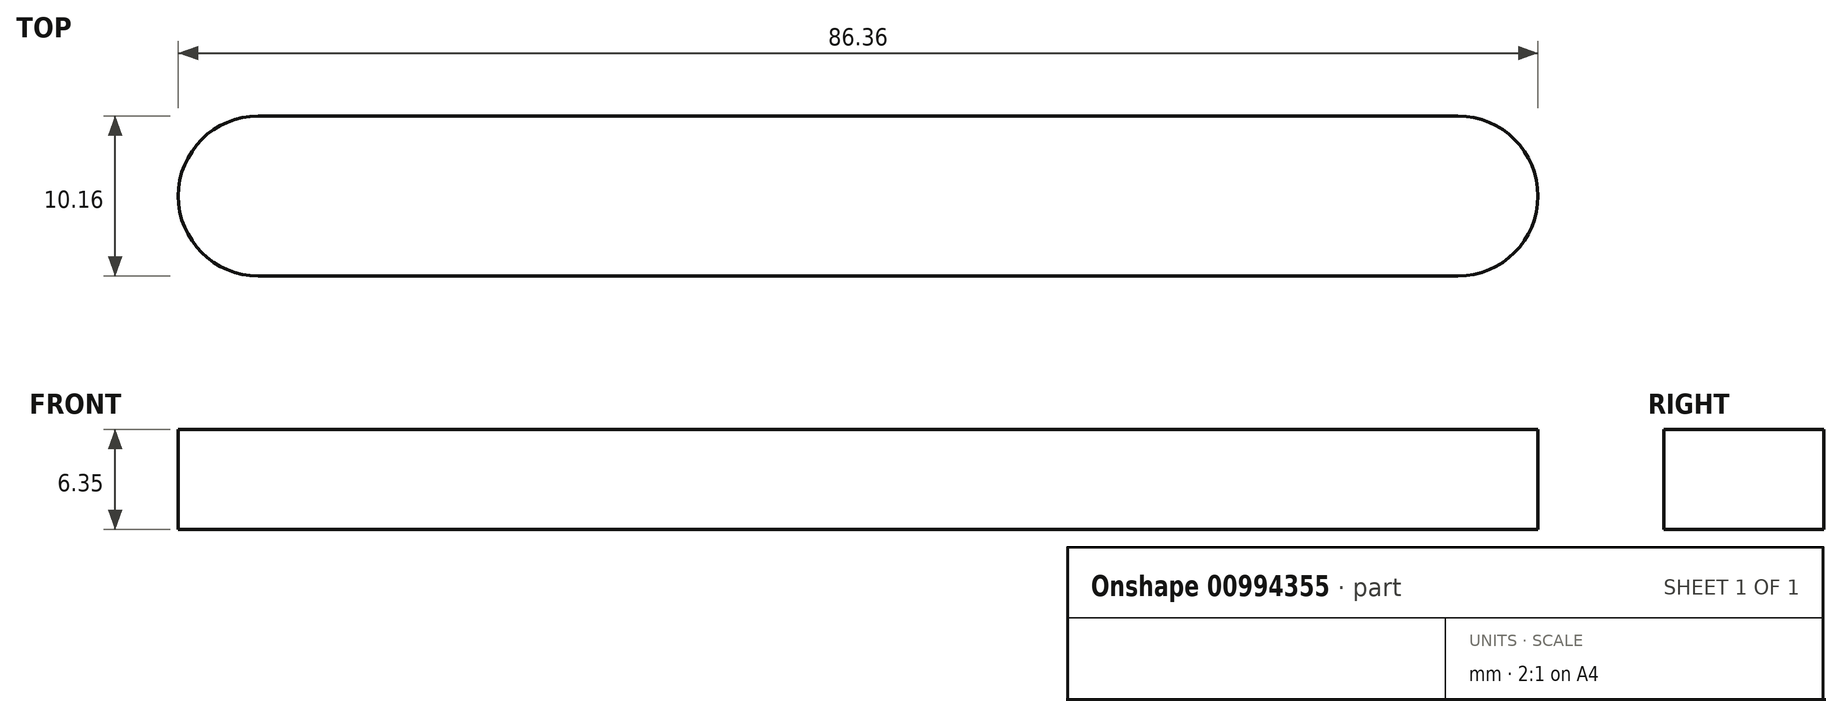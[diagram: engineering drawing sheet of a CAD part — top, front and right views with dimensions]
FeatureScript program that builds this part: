
annotation { "Feature Type Name" : "Feature", "Feature Type Description" : "" }
export const myFeature = defineFeature(function(context is Context, id is Id, definition is map)
    precondition{}
    {
        {
            var Q0;
            Q0=qCreatedBy(makeId("Top.planeOp"),FACE);
            var sketch = newSketch(context, id + "F0", { "sketchPlane" : qUnion([Q0])});
            skLineSegment(sketch, "E0.bottom", {"start": v(-50.8, 12.7) * mm, "end": v(50.8, 12.7) * mm});
            skLineSegment(sketch, "E0.top", {"start": v(-50.8, -12.7) * mm, "end": v(50.8, -12.7) * mm});
            skLineSegment(sketch, "E0.left", {"start": v(-50.8, 12.7) * mm, "end": v(-50.8, -12.7) * mm});
            skLineSegment(sketch, "E0.right", {"start": v(50.8, 12.7) * mm, "end": v(50.8, -12.7) * mm});
            skLineSegment(sketch, "E1", {"start": v(-50.8, 12.7) * mm, "end": v(50.8, -12.7) * mm, "construction": true});
            skSolve(sketch);
        }
        {
            var Q0;
            Q0=makeQuery(id+"F0.imprint","IMPRINT",FACE,{"disambiguationData":[TD([[makeQuery(id+"F0.imprint","IMPRINT",EDGE,{"derivedFrom":sQuery(id+"F0.wireOp",EDGE,"E0.bottom")}),-1.0]])]});
            extrude(context, id + "F1", {"entities" : qUnion([Q0]), "depth" : 6.35 * mm, "offsetDistance" : 25.4 * mm});
        }
        {
            var Q0;
            Q0=makeQuery(id+"F1.opExtrude","CAP_FACE",FACE,{"disambiguationData":[OSD([sQuery(id+"F0.wireOp",EDGE,"E0.bottom"),sQuery(id+"F0.wireOp",EDGE,"E0.top"),sQuery(id+"F0.wireOp",EDGE,"E0.left"),sQuery(id+"F0.wireOp",EDGE,"E0.right")])],"isStart":false});
            chamfer(context, id + "F2", {"entities" : qUnion([Q0]), "chamferType" : ChamferType.OFFSET_ANGLE, "width" : 6.35 * mm, "oppositeDirection" : false, "angle" : 30 * degree, "tangentPropagation" : true});
        }
        {
            var Q0;
            Q0 = qSketchRegion(id + "F0", true);
            var sketch = newSketch(context, id + "F3", { "sketchPlane" : qUnion([Q0])});
            skLineSegment(sketch, "E2", {"start": v(-38.1, 0) * mm, "end": v(38.1, 0) * mm});
            skArc(sketch, "E3.0.startCap", {"start": v(-38.1, -5.08) * mm, "mid": v(-43.18, 0) * mm, "end": v(-38.1, 5.08) * mm});
            skArc(sketch, "E3.0.endCap", {"start": v(38.1, 5.08) * mm, "mid": v(43.18, 0) * mm, "end": v(38.1, -5.08) * mm});
            skLineSegment(sketch, "E3.0.left", {"start": v(-38.1, 5.08) * mm, "end": v(38.1, 5.08) * mm});
            skLineSegment(sketch, "E3.0.right", {"start": v(-38.1, -5.08) * mm, "end": v(38.1, -5.08) * mm});
            skSolve(sketch);
        }
        {
            var Q0;
            Q0=makeQuery(id+"F3.imprint","IMPRINT",FACE,{"disambiguationData":[TD([[makeQuery(id+"F3.imprint","IMPRINT",EDGE,{"derivedFrom":sQuery(id+"F3.wireOp",EDGE,"E3.0.startCap")}),-1.0]])]});
            extrude(context, id + "F4", {"entities" : qUnion([Q0]), "operationType" : NewBodyOperationType.REMOVE, "depth" : 42.23 * mm, "offsetDistance" : 25.4 * mm});
        }
    });
